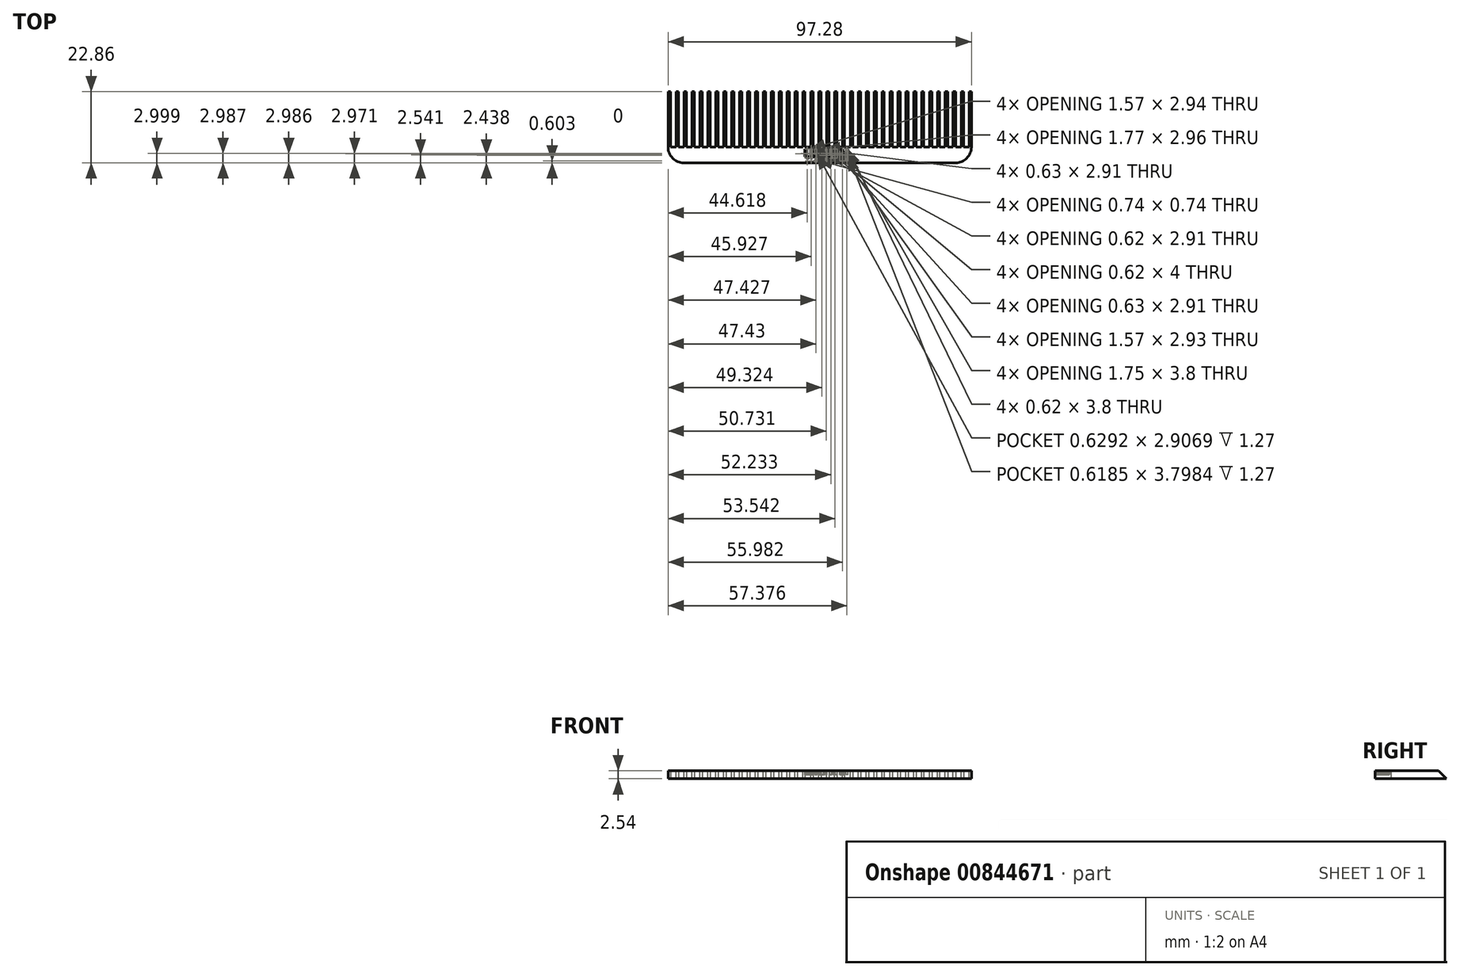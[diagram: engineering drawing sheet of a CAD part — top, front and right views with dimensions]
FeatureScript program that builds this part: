
annotation { "Feature Type Name" : "Feature", "Feature Type Description" : "" }
export const myFeature = defineFeature(function(context is Context, id is Id, definition is map)
    precondition{}
    {
        {
            var Q0;
            Q0=qCreatedBy(makeId("Top.planeOp"),FACE);
            var sketch = newSketch(context, id + "F0", { "sketchPlane" : qUnion([Q0])});
            skLineSegment(sketch, "E0.bottom", {"start": v(46.48, -2.54) * mm, "end": v(-50.8, -2.54) * mm});
            skLineSegment(sketch, "E0.top", {"start": v(46.48, 2.54) * mm, "end": v(-50.8, 2.54) * mm});
            skLineSegment(sketch, "E0.right", {"start": v(-50.8, -2.54) * mm, "end": v(-50.8, 2.54) * mm});
            skPoint(sketch, "E0.middle", {"position": v(0, 0) * mm});
            skLineSegment(sketch, "E1.bottom", {"start": v(-50.8, 2.54) * mm, "end": v(-50.04, 2.54) * mm});
            skLineSegment(sketch, "E1.top", {"start": v(-50.8, 22.86) * mm, "end": v(-50.04, 22.86) * mm});
            skLineSegment(sketch, "E1.left", {"start": v(-50.8, 2.54) * mm, "end": v(-50.8, 22.86) * mm});
            skLineSegment(sketch, "E1.right", {"start": v(-50.04, 2.54) * mm, "end": v(-50.04, 22.86) * mm});
            skLineSegment(sketch, "E2.1.0.0", {"start": v(-47.5, 2.54) * mm, "end": v(-47.5, 22.86) * mm});
            skLineSegment(sketch, "E2.1.0.1", {"start": v(-48.26, 2.54) * mm, "end": v(-48.26, 22.86) * mm});
            skLineSegment(sketch, "E2.1.0.2", {"start": v(-48.26, 22.86) * mm, "end": v(-47.5, 22.86) * mm});
            skLineSegment(sketch, "E2.2.0.0", {"start": v(-44.96, 2.54) * mm, "end": v(-44.96, 22.86) * mm});
            skLineSegment(sketch, "E2.2.0.1", {"start": v(-45.72, 2.54) * mm, "end": v(-45.72, 22.86) * mm});
            skLineSegment(sketch, "E2.2.0.2", {"start": v(-45.72, 22.86) * mm, "end": v(-44.96, 22.86) * mm});
            skLineSegment(sketch, "E2.3.0.0", {"start": v(-42.42, 2.54) * mm, "end": v(-42.42, 22.86) * mm});
            skLineSegment(sketch, "E2.3.0.1", {"start": v(-43.18, 2.54) * mm, "end": v(-43.18, 22.86) * mm});
            skLineSegment(sketch, "E2.3.0.2", {"start": v(-43.18, 22.86) * mm, "end": v(-42.42, 22.86) * mm});
            skLineSegment(sketch, "E2.4.0.0", {"start": v(-39.88, 2.54) * mm, "end": v(-39.88, 22.86) * mm});
            skLineSegment(sketch, "E2.4.0.1", {"start": v(-40.64, 2.54) * mm, "end": v(-40.64, 22.86) * mm});
            skLineSegment(sketch, "E2.4.0.2", {"start": v(-40.64, 22.86) * mm, "end": v(-39.88, 22.86) * mm});
            skLineSegment(sketch, "E2.5.0.0", {"start": v(-37.34, 2.54) * mm, "end": v(-37.34, 22.86) * mm});
            skLineSegment(sketch, "E2.5.0.1", {"start": v(-38.1, 2.54) * mm, "end": v(-38.1, 22.86) * mm});
            skLineSegment(sketch, "E2.5.0.2", {"start": v(-38.1, 22.86) * mm, "end": v(-37.34, 22.86) * mm});
            skLineSegment(sketch, "E2.6.0.0", {"start": v(-34.8, 2.54) * mm, "end": v(-34.8, 22.86) * mm});
            skLineSegment(sketch, "E2.6.0.1", {"start": v(-35.56, 2.54) * mm, "end": v(-35.56, 22.86) * mm});
            skLineSegment(sketch, "E2.6.0.2", {"start": v(-35.56, 22.86) * mm, "end": v(-34.8, 22.86) * mm});
            skLineSegment(sketch, "E2.7.0.0", {"start": v(-32.26, 2.54) * mm, "end": v(-32.26, 22.86) * mm});
            skLineSegment(sketch, "E2.7.0.1", {"start": v(-33.02, 2.54) * mm, "end": v(-33.02, 22.86) * mm});
            skLineSegment(sketch, "E2.7.0.2", {"start": v(-33.02, 22.86) * mm, "end": v(-32.26, 22.86) * mm});
            skLineSegment(sketch, "E2.8.0.0", {"start": v(-29.72, 2.54) * mm, "end": v(-29.72, 22.86) * mm});
            skLineSegment(sketch, "E2.8.0.1", {"start": v(-30.48, 2.54) * mm, "end": v(-30.48, 22.86) * mm});
            skLineSegment(sketch, "E2.8.0.2", {"start": v(-30.48, 22.86) * mm, "end": v(-29.72, 22.86) * mm});
            skLineSegment(sketch, "E2.9.0.0", {"start": v(-27.18, 2.54) * mm, "end": v(-27.18, 22.86) * mm});
            skLineSegment(sketch, "E2.9.0.1", {"start": v(-27.94, 2.54) * mm, "end": v(-27.94, 22.86) * mm});
            skLineSegment(sketch, "E2.9.0.2", {"start": v(-27.94, 22.86) * mm, "end": v(-27.18, 22.86) * mm});
            skLineSegment(sketch, "E2.direction1", {"start": v(-50.04, 2.54) * mm, "end": v(-47.5, 2.54) * mm, "construction": true});
            skLineSegment(sketch, "E3.1.0.0", {"start": v(-25.4, 2.54) * mm, "end": v(-25.4, 22.86) * mm});
            skLineSegment(sketch, "E3.1.0.1", {"start": v(-24.64, 2.54) * mm, "end": v(-24.64, 22.86) * mm});
            skLineSegment(sketch, "E3.1.0.2", {"start": v(-25.4, 22.86) * mm, "end": v(-24.64, 22.86) * mm});
            skLineSegment(sketch, "E3.2.0.0", {"start": v(-22.86, 2.54) * mm, "end": v(-22.86, 22.86) * mm});
            skLineSegment(sketch, "E3.2.0.1", {"start": v(-22.1, 2.54) * mm, "end": v(-22.1, 22.86) * mm});
            skLineSegment(sketch, "E3.2.0.2", {"start": v(-22.86, 22.86) * mm, "end": v(-22.1, 22.86) * mm});
            skLineSegment(sketch, "E3.3.0.0", {"start": v(-20.32, 2.54) * mm, "end": v(-20.32, 22.86) * mm});
            skLineSegment(sketch, "E3.3.0.1", {"start": v(-19.56, 2.54) * mm, "end": v(-19.56, 22.86) * mm});
            skLineSegment(sketch, "E3.3.0.2", {"start": v(-20.32, 22.86) * mm, "end": v(-19.56, 22.86) * mm});
            skLineSegment(sketch, "E3.4.0.0", {"start": v(-17.78, 2.54) * mm, "end": v(-17.78, 22.86) * mm});
            skLineSegment(sketch, "E3.4.0.1", {"start": v(-17.02, 2.54) * mm, "end": v(-17.02, 22.86) * mm});
            skLineSegment(sketch, "E3.4.0.2", {"start": v(-17.78, 22.86) * mm, "end": v(-17.02, 22.86) * mm});
            skLineSegment(sketch, "E3.5.0.0", {"start": v(-15.24, 2.54) * mm, "end": v(-15.24, 22.86) * mm});
            skLineSegment(sketch, "E3.5.0.1", {"start": v(-14.48, 2.54) * mm, "end": v(-14.48, 22.86) * mm});
            skLineSegment(sketch, "E3.5.0.2", {"start": v(-15.24, 22.86) * mm, "end": v(-14.48, 22.86) * mm});
            skLineSegment(sketch, "E3.6.0.0", {"start": v(-12.7, 2.54) * mm, "end": v(-12.7, 22.86) * mm});
            skLineSegment(sketch, "E3.6.0.1", {"start": v(-11.94, 2.54) * mm, "end": v(-11.94, 22.86) * mm});
            skLineSegment(sketch, "E3.6.0.2", {"start": v(-12.7, 22.86) * mm, "end": v(-11.94, 22.86) * mm});
            skLineSegment(sketch, "E3.7.0.0", {"start": v(-10.16, 2.54) * mm, "end": v(-10.16, 22.86) * mm});
            skLineSegment(sketch, "E3.7.0.1", {"start": v(-9.4, 2.54) * mm, "end": v(-9.4, 22.86) * mm});
            skLineSegment(sketch, "E3.7.0.2", {"start": v(-10.16, 22.86) * mm, "end": v(-9.4, 22.86) * mm});
            skLineSegment(sketch, "E3.8.0.0", {"start": v(-7.62, 2.54) * mm, "end": v(-7.62, 22.86) * mm});
            skLineSegment(sketch, "E3.8.0.1", {"start": v(-6.86, 2.54) * mm, "end": v(-6.86, 22.86) * mm});
            skLineSegment(sketch, "E3.8.0.2", {"start": v(-7.62, 22.86) * mm, "end": v(-6.86, 22.86) * mm});
            skLineSegment(sketch, "E3.9.0.0", {"start": v(-5.08, 2.54) * mm, "end": v(-5.08, 22.86) * mm});
            skLineSegment(sketch, "E3.9.0.1", {"start": v(-4.32, 2.54) * mm, "end": v(-4.32, 22.86) * mm});
            skLineSegment(sketch, "E3.9.0.2", {"start": v(-5.08, 22.86) * mm, "end": v(-4.32, 22.86) * mm});
            skLineSegment(sketch, "E3.direction1", {"start": v(-27.94, 2.54) * mm, "end": v(-25.4, 2.54) * mm, "construction": true});
            skLineSegment(sketch, "E4.1.0.0", {"start": v(-1.78, 2.54) * mm, "end": v(-1.78, 22.86) * mm});
            skLineSegment(sketch, "E4.1.0.1", {"start": v(-2.54, 2.54) * mm, "end": v(-2.54, 22.86) * mm});
            skLineSegment(sketch, "E4.1.0.2", {"start": v(-2.54, 22.86) * mm, "end": v(-1.78, 22.86) * mm});
            skLineSegment(sketch, "E4.2.0.0", {"start": v(0.76, 2.54) * mm, "end": v(0.76, 22.86) * mm});
            skLineSegment(sketch, "E4.2.0.1", {"start": v(0, 2.54) * mm, "end": v(0, 22.86) * mm});
            skLineSegment(sketch, "E4.2.0.2", {"start": v(0, 22.86) * mm, "end": v(0.76, 22.86) * mm});
            skLineSegment(sketch, "E4.3.0.0", {"start": v(3.3, 2.54) * mm, "end": v(3.3, 22.86) * mm});
            skLineSegment(sketch, "E4.3.0.1", {"start": v(2.54, 2.54) * mm, "end": v(2.54, 22.86) * mm});
            skLineSegment(sketch, "E4.3.0.2", {"start": v(2.54, 22.86) * mm, "end": v(3.3, 22.86) * mm});
            skLineSegment(sketch, "E4.4.0.0", {"start": v(5.84, 2.54) * mm, "end": v(5.84, 22.86) * mm});
            skLineSegment(sketch, "E4.4.0.1", {"start": v(5.08, 2.54) * mm, "end": v(5.08, 22.86) * mm});
            skLineSegment(sketch, "E4.4.0.2", {"start": v(5.08, 22.86) * mm, "end": v(5.84, 22.86) * mm});
            skLineSegment(sketch, "E4.5.0.0", {"start": v(8.38, 2.54) * mm, "end": v(8.38, 22.86) * mm});
            skLineSegment(sketch, "E4.5.0.1", {"start": v(7.62, 2.54) * mm, "end": v(7.62, 22.86) * mm});
            skLineSegment(sketch, "E4.5.0.2", {"start": v(7.62, 22.86) * mm, "end": v(8.38, 22.86) * mm});
            skLineSegment(sketch, "E4.6.0.0", {"start": v(10.92, 2.54) * mm, "end": v(10.92, 22.86) * mm});
            skLineSegment(sketch, "E4.6.0.1", {"start": v(10.16, 2.54) * mm, "end": v(10.16, 22.86) * mm});
            skLineSegment(sketch, "E4.6.0.2", {"start": v(10.16, 22.86) * mm, "end": v(10.92, 22.86) * mm});
            skLineSegment(sketch, "E4.7.0.0", {"start": v(13.46, 2.54) * mm, "end": v(13.46, 22.86) * mm});
            skLineSegment(sketch, "E4.7.0.1", {"start": v(12.7, 2.54) * mm, "end": v(12.7, 22.86) * mm});
            skLineSegment(sketch, "E4.7.0.2", {"start": v(12.7, 22.86) * mm, "end": v(13.46, 22.86) * mm});
            skLineSegment(sketch, "E4.8.0.0", {"start": v(16, 2.54) * mm, "end": v(16, 22.86) * mm});
            skLineSegment(sketch, "E4.8.0.1", {"start": v(15.24, 2.54) * mm, "end": v(15.24, 22.86) * mm});
            skLineSegment(sketch, "E4.8.0.2", {"start": v(15.24, 22.86) * mm, "end": v(16, 22.86) * mm});
            skLineSegment(sketch, "E4.9.0.0", {"start": v(18.54, 2.54) * mm, "end": v(18.54, 22.86) * mm});
            skLineSegment(sketch, "E4.9.0.1", {"start": v(17.78, 2.54) * mm, "end": v(17.78, 22.86) * mm});
            skLineSegment(sketch, "E4.9.0.2", {"start": v(17.78, 22.86) * mm, "end": v(18.54, 22.86) * mm});
            skLineSegment(sketch, "E4.direction1", {"start": v(-4.32, 2.54) * mm, "end": v(-1.78, 2.54) * mm, "construction": true});
            skLineSegment(sketch, "E5.1.0.0", {"start": v(21.08, 2.54) * mm, "end": v(21.08, 22.86) * mm});
            skLineSegment(sketch, "E5.1.0.1", {"start": v(20.32, 2.54) * mm, "end": v(20.32, 22.86) * mm});
            skLineSegment(sketch, "E5.1.0.2", {"start": v(20.32, 22.86) * mm, "end": v(21.08, 22.86) * mm});
            skLineSegment(sketch, "E5.2.0.0", {"start": v(23.62, 2.54) * mm, "end": v(23.62, 22.86) * mm});
            skLineSegment(sketch, "E5.2.0.1", {"start": v(22.86, 2.54) * mm, "end": v(22.86, 22.86) * mm});
            skLineSegment(sketch, "E5.2.0.2", {"start": v(22.86, 22.86) * mm, "end": v(23.62, 22.86) * mm});
            skLineSegment(sketch, "E5.2.0.3", {"start": v(21.08, 2.54) * mm, "end": v(21.08, 22.86) * mm});
            skLineSegment(sketch, "E5.2.0.4", {"start": v(20.32, 2.54) * mm, "end": v(20.32, 22.86) * mm});
            skLineSegment(sketch, "E5.2.0.5", {"start": v(20.32, 22.86) * mm, "end": v(21.08, 22.86) * mm});
            skLineSegment(sketch, "E5.3.0.0", {"start": v(26.16, 2.54) * mm, "end": v(26.16, 22.86) * mm});
            skLineSegment(sketch, "E5.3.0.1", {"start": v(25.4, 2.54) * mm, "end": v(25.4, 22.86) * mm});
            skLineSegment(sketch, "E5.3.0.2", {"start": v(25.4, 22.86) * mm, "end": v(26.16, 22.86) * mm});
            skLineSegment(sketch, "E5.3.0.3", {"start": v(23.62, 2.54) * mm, "end": v(23.62, 22.86) * mm});
            skLineSegment(sketch, "E5.3.0.4", {"start": v(22.86, 2.54) * mm, "end": v(22.86, 22.86) * mm});
            skLineSegment(sketch, "E5.3.0.5", {"start": v(22.86, 22.86) * mm, "end": v(23.62, 22.86) * mm});
            skLineSegment(sketch, "E5.3.0.6", {"start": v(21.08, 2.54) * mm, "end": v(21.08, 22.86) * mm});
            skLineSegment(sketch, "E5.3.0.7", {"start": v(20.32, 2.54) * mm, "end": v(20.32, 22.86) * mm});
            skLineSegment(sketch, "E5.3.0.8", {"start": v(20.32, 22.86) * mm, "end": v(21.08, 22.86) * mm});
            skLineSegment(sketch, "E5.4.0.0", {"start": v(28.7, 2.54) * mm, "end": v(28.7, 22.86) * mm});
            skLineSegment(sketch, "E5.4.0.1", {"start": v(27.94, 2.54) * mm, "end": v(27.94, 22.86) * mm});
            skLineSegment(sketch, "E5.4.0.2", {"start": v(27.94, 22.86) * mm, "end": v(28.7, 22.86) * mm});
            skLineSegment(sketch, "E5.4.0.3", {"start": v(26.16, 2.54) * mm, "end": v(26.16, 22.86) * mm});
            skLineSegment(sketch, "E5.4.0.4", {"start": v(25.4, 2.54) * mm, "end": v(25.4, 22.86) * mm});
            skLineSegment(sketch, "E5.4.0.5", {"start": v(25.4, 22.86) * mm, "end": v(26.16, 22.86) * mm});
            skLineSegment(sketch, "E5.4.0.6", {"start": v(23.62, 2.54) * mm, "end": v(23.62, 22.86) * mm});
            skLineSegment(sketch, "E5.4.0.7", {"start": v(22.86, 2.54) * mm, "end": v(22.86, 22.86) * mm});
            skLineSegment(sketch, "E5.4.0.8", {"start": v(22.86, 22.86) * mm, "end": v(23.62, 22.86) * mm});
            skLineSegment(sketch, "E5.5.0.0", {"start": v(31.24, 2.54) * mm, "end": v(31.24, 22.86) * mm});
            skLineSegment(sketch, "E5.5.0.1", {"start": v(30.48, 2.54) * mm, "end": v(30.48, 22.86) * mm});
            skLineSegment(sketch, "E5.5.0.2", {"start": v(30.48, 22.86) * mm, "end": v(31.24, 22.86) * mm});
            skLineSegment(sketch, "E5.5.0.3", {"start": v(28.7, 2.54) * mm, "end": v(28.7, 22.86) * mm});
            skLineSegment(sketch, "E5.5.0.4", {"start": v(27.94, 2.54) * mm, "end": v(27.94, 22.86) * mm});
            skLineSegment(sketch, "E5.5.0.5", {"start": v(27.94, 22.86) * mm, "end": v(28.7, 22.86) * mm});
            skLineSegment(sketch, "E5.5.0.6", {"start": v(26.16, 2.54) * mm, "end": v(26.16, 22.86) * mm});
            skLineSegment(sketch, "E5.5.0.7", {"start": v(25.4, 2.54) * mm, "end": v(25.4, 22.86) * mm});
            skLineSegment(sketch, "E5.5.0.8", {"start": v(25.4, 22.86) * mm, "end": v(26.16, 22.86) * mm});
            skLineSegment(sketch, "E5.6.0.0", {"start": v(33.78, 2.54) * mm, "end": v(33.78, 22.86) * mm});
            skLineSegment(sketch, "E5.6.0.1", {"start": v(33.02, 2.54) * mm, "end": v(33.02, 22.86) * mm});
            skLineSegment(sketch, "E5.6.0.2", {"start": v(33.02, 22.86) * mm, "end": v(33.78, 22.86) * mm});
            skLineSegment(sketch, "E5.6.0.3", {"start": v(31.24, 2.54) * mm, "end": v(31.24, 22.86) * mm});
            skLineSegment(sketch, "E5.6.0.4", {"start": v(30.48, 2.54) * mm, "end": v(30.48, 22.86) * mm});
            skLineSegment(sketch, "E5.6.0.5", {"start": v(30.48, 22.86) * mm, "end": v(31.24, 22.86) * mm});
            skLineSegment(sketch, "E5.6.0.6", {"start": v(28.7, 2.54) * mm, "end": v(28.7, 22.86) * mm});
            skLineSegment(sketch, "E5.6.0.7", {"start": v(27.94, 2.54) * mm, "end": v(27.94, 22.86) * mm});
            skLineSegment(sketch, "E5.6.0.8", {"start": v(27.94, 22.86) * mm, "end": v(28.7, 22.86) * mm});
            skLineSegment(sketch, "E5.7.0.0", {"start": v(36.32, 2.54) * mm, "end": v(36.32, 22.86) * mm});
            skLineSegment(sketch, "E5.7.0.1", {"start": v(35.56, 2.54) * mm, "end": v(35.56, 22.86) * mm});
            skLineSegment(sketch, "E5.7.0.2", {"start": v(35.56, 22.86) * mm, "end": v(36.32, 22.86) * mm});
            skLineSegment(sketch, "E5.7.0.3", {"start": v(33.78, 2.54) * mm, "end": v(33.78, 22.86) * mm});
            skLineSegment(sketch, "E5.7.0.4", {"start": v(33.02, 2.54) * mm, "end": v(33.02, 22.86) * mm});
            skLineSegment(sketch, "E5.7.0.5", {"start": v(33.02, 22.86) * mm, "end": v(33.78, 22.86) * mm});
            skLineSegment(sketch, "E5.7.0.6", {"start": v(31.24, 2.54) * mm, "end": v(31.24, 22.86) * mm});
            skLineSegment(sketch, "E5.7.0.7", {"start": v(30.48, 2.54) * mm, "end": v(30.48, 22.86) * mm});
            skLineSegment(sketch, "E5.7.0.8", {"start": v(30.48, 22.86) * mm, "end": v(31.24, 22.86) * mm});
            skLineSegment(sketch, "E5.8.0.0", {"start": v(38.86, 2.54) * mm, "end": v(38.86, 22.86) * mm});
            skLineSegment(sketch, "E5.8.0.1", {"start": v(38.1, 2.54) * mm, "end": v(38.1, 22.86) * mm});
            skLineSegment(sketch, "E5.8.0.2", {"start": v(38.1, 22.86) * mm, "end": v(38.86, 22.86) * mm});
            skLineSegment(sketch, "E5.8.0.3", {"start": v(36.32, 2.54) * mm, "end": v(36.32, 22.86) * mm});
            skLineSegment(sketch, "E5.8.0.4", {"start": v(35.56, 2.54) * mm, "end": v(35.56, 22.86) * mm});
            skLineSegment(sketch, "E5.8.0.5", {"start": v(35.56, 22.86) * mm, "end": v(36.32, 22.86) * mm});
            skLineSegment(sketch, "E5.8.0.6", {"start": v(33.78, 2.54) * mm, "end": v(33.78, 22.86) * mm});
            skLineSegment(sketch, "E5.8.0.7", {"start": v(33.02, 2.54) * mm, "end": v(33.02, 22.86) * mm});
            skLineSegment(sketch, "E5.8.0.8", {"start": v(33.02, 22.86) * mm, "end": v(33.78, 22.86) * mm});
            skLineSegment(sketch, "E5.9.0.0", {"start": v(41.4, 2.54) * mm, "end": v(41.4, 22.86) * mm});
            skLineSegment(sketch, "E5.9.0.1", {"start": v(40.64, 2.54) * mm, "end": v(40.64, 22.86) * mm});
            skLineSegment(sketch, "E5.9.0.2", {"start": v(40.64, 22.86) * mm, "end": v(41.4, 22.86) * mm});
            skLineSegment(sketch, "E5.9.0.3", {"start": v(38.86, 2.54) * mm, "end": v(38.86, 22.86) * mm});
            skLineSegment(sketch, "E5.9.0.4", {"start": v(38.1, 2.54) * mm, "end": v(38.1, 22.86) * mm});
            skLineSegment(sketch, "E5.9.0.5", {"start": v(38.1, 22.86) * mm, "end": v(38.86, 22.86) * mm});
            skLineSegment(sketch, "E5.9.0.6", {"start": v(36.32, 2.54) * mm, "end": v(36.32, 22.86) * mm});
            skLineSegment(sketch, "E5.9.0.7", {"start": v(35.56, 2.54) * mm, "end": v(35.56, 22.86) * mm});
            skLineSegment(sketch, "E5.9.0.8", {"start": v(35.56, 22.86) * mm, "end": v(36.32, 22.86) * mm});
            skLineSegment(sketch, "E5.direction1", {"start": v(18.54, 2.54) * mm, "end": v(21.08, 2.54) * mm, "construction": true});
            skLineSegment(sketch, "E6.1.0.0", {"start": v(43.94, 2.54) * mm, "end": v(43.94, 22.86) * mm});
            skLineSegment(sketch, "E6.1.0.1", {"start": v(43.18, 2.54) * mm, "end": v(43.18, 22.86) * mm});
            skLineSegment(sketch, "E6.1.0.2", {"start": v(43.18, 22.86) * mm, "end": v(43.94, 22.86) * mm});
            skLineSegment(sketch, "E6.2.0.0", {"start": v(46.48, 2.54) * mm, "end": v(46.48, 22.86) * mm});
            skLineSegment(sketch, "E6.2.0.1", {"start": v(45.72, 2.54) * mm, "end": v(45.72, 22.86) * mm});
            skLineSegment(sketch, "E6.2.0.2", {"start": v(45.72, 22.86) * mm, "end": v(46.48, 22.86) * mm});
            skLineSegment(sketch, "E6.direction1", {"start": v(41.4, 2.54) * mm, "end": v(43.94, 2.54) * mm, "construction": true});
            skLineSegment(sketch, "E7", {"start": v(46.48, 2.54) * mm, "end": v(46.48, -2.54) * mm});
            skPoint(sketch, "E0.left.end.orphan", {"position": v(50.8, 2.54) * mm});
            skPoint(sketch, "E8.orphan", {"position": v(50.8, -2.54) * mm});
            skSolve(sketch);
        }
        {
            var Q0;
            {var subQ0=sQuery(id+"F0.wireOp",EDGE,"E4.4.0.0");Q0=makeQuery(id+"F0.imprint","IMPRINT",FACE,{"disambiguationData":[TD([[makeQuery(id+"F0.imprint","IMPRINT",EDGE,{"derivedFrom":subQ0}),1.0]])]});}
            var Q1;
            {var subQ0=sQuery(id+"F0.wireOp",EDGE,"E6.1.0.0");Q1=makeQuery(id+"F0.imprint","IMPRINT",FACE,{"disambiguationData":[TD([[makeQuery(id+"F0.imprint","IMPRINT",EDGE,{"derivedFrom":subQ0}),1.0]])]});}
            var Q2;
            {var subQ0=sQuery(id+"F0.wireOp",EDGE,"E3.2.0.0");Q2=makeQuery(id+"F0.imprint","IMPRINT",FACE,{"disambiguationData":[TD([[makeQuery(id+"F0.imprint","IMPRINT",EDGE,{"derivedFrom":subQ0}),-1.0]])]});}
            var Q3;
            {var subQ0=sQuery(id+"F0.wireOp",EDGE,"E6.2.0.0");Q3=makeQuery(id+"F0.imprint","IMPRINT",FACE,{"disambiguationData":[TD([[makeQuery(id+"F0.imprint","IMPRINT",EDGE,{"derivedFrom":subQ0}),1.0]])]});}
            var Q4;
            {var subQ0=sQuery(id+"F0.wireOp",EDGE,"E2.3.0.0");Q4=makeQuery(id+"F0.imprint","IMPRINT",FACE,{"disambiguationData":[TD([[makeQuery(id+"F0.imprint","IMPRINT",EDGE,{"derivedFrom":subQ0}),1.0]])]});}
            var Q5;
            {var subQ0=sQuery(id+"F0.wireOp",EDGE,"E5.8.0.0");Q5=makeQuery(id+"F0.imprint","IMPRINT",FACE,{"disambiguationData":[TD([[makeQuery(id+"F0.imprint","IMPRINT",EDGE,{"derivedFrom":subQ0}),1.0]])]});}
            var Q6;
            {var subQ0=sQuery(id+"F0.wireOp",EDGE,"E2.6.0.0");Q6=makeQuery(id+"F0.imprint","IMPRINT",FACE,{"disambiguationData":[TD([[makeQuery(id+"F0.imprint","IMPRINT",EDGE,{"derivedFrom":subQ0}),1.0]])]});}
            var Q7;
            Q7=makeQuery(id+"F0.imprint","IMPRINT",FACE,{"disambiguationData":[TD([[makeQuery(id+"F0.imprint","IMPRINT",EDGE,{"derivedFrom":sQuery(id+"F0.wireOp",EDGE,"E1.top")}),-1.0]])]});
            var Q8;
            {var subQ0=sQuery(id+"F0.wireOp",EDGE,"E5.6.0.0");Q8=makeQuery(id+"F0.imprint","IMPRINT",FACE,{"disambiguationData":[TD([[makeQuery(id+"F0.imprint","IMPRINT",EDGE,{"derivedFrom":subQ0}),1.0]])]});}
            var Q9;
            {var subQ0=sQuery(id+"F0.wireOp",EDGE,"E3.1.0.0");Q9=makeQuery(id+"F0.imprint","IMPRINT",FACE,{"disambiguationData":[TD([[makeQuery(id+"F0.imprint","IMPRINT",EDGE,{"derivedFrom":subQ0}),-1.0]])]});}
            var Q10;
            {var subQ0=sQuery(id+"F0.wireOp",EDGE,"E3.3.0.0");Q10=makeQuery(id+"F0.imprint","IMPRINT",FACE,{"disambiguationData":[TD([[makeQuery(id+"F0.imprint","IMPRINT",EDGE,{"derivedFrom":subQ0}),-1.0]])]});}
            var Q11;
            {var subQ2=sQuery(id+"F0.wireOp",EDGE,"E2.1.0.0");Q11=makeQuery(id+"F0.imprint","IMPRINT",FACE,{"disambiguationData":[TD([[makeQuery(id+"F0.imprint","IMPRINT",EDGE,{"derivedFrom":subQ2}),1.0]])]});}
            var Q12;
            {var subQ0=sQuery(id+"F0.wireOp",EDGE,"E2.9.0.0");Q12=makeQuery(id+"F0.imprint","IMPRINT",FACE,{"disambiguationData":[TD([[makeQuery(id+"F0.imprint","IMPRINT",EDGE,{"derivedFrom":subQ0}),1.0]])]});}
            var Q13;
            {var subQ0=sQuery(id+"F0.wireOp",EDGE,"E2.4.0.0");Q13=makeQuery(id+"F0.imprint","IMPRINT",FACE,{"disambiguationData":[TD([[makeQuery(id+"F0.imprint","IMPRINT",EDGE,{"derivedFrom":subQ0}),1.0]])]});}
            var Q14;
            Q14=makeQuery(id+"F0.imprint","IMPRINT",FACE,{"disambiguationData":[TD([[makeQuery(id+"F0.imprint","IMPRINT",EDGE,{"derivedFrom":sQuery(id+"F0.wireOp",EDGE,"E0.bottom")}),-1.0]])]});
            var Q15;
            {var subQ0=sQuery(id+"F0.wireOp",EDGE,"E2.5.0.0");Q15=makeQuery(id+"F0.imprint","IMPRINT",FACE,{"disambiguationData":[TD([[makeQuery(id+"F0.imprint","IMPRINT",EDGE,{"derivedFrom":subQ0}),1.0]])]});}
            var Q16;
            {var subQ0=sQuery(id+"F0.wireOp",EDGE,"E2.8.0.0");Q16=makeQuery(id+"F0.imprint","IMPRINT",FACE,{"disambiguationData":[TD([[makeQuery(id+"F0.imprint","IMPRINT",EDGE,{"derivedFrom":subQ0}),1.0]])]});}
            var Q17;
            {var subQ0=sQuery(id+"F0.wireOp",EDGE,"E2.2.0.0");Q17=makeQuery(id+"F0.imprint","IMPRINT",FACE,{"disambiguationData":[TD([[makeQuery(id+"F0.imprint","IMPRINT",EDGE,{"derivedFrom":subQ0}),1.0]])]});}
            var Q18;
            {var subQ0=sQuery(id+"F0.wireOp",EDGE,"E3.4.0.0");Q18=makeQuery(id+"F0.imprint","IMPRINT",FACE,{"disambiguationData":[TD([[makeQuery(id+"F0.imprint","IMPRINT",EDGE,{"derivedFrom":subQ0}),-1.0]])]});}
            var Q19;
            {var subQ0=sQuery(id+"F0.wireOp",EDGE,"E4.7.0.0");Q19=makeQuery(id+"F0.imprint","IMPRINT",FACE,{"disambiguationData":[TD([[makeQuery(id+"F0.imprint","IMPRINT",EDGE,{"derivedFrom":subQ0}),1.0]])]});}
            var Q20;
            {var subQ2=sQuery(id+"F0.wireOp",EDGE,"E2.7.0.0");Q20=makeQuery(id+"F0.imprint","IMPRINT",FACE,{"disambiguationData":[TD([[makeQuery(id+"F0.imprint","IMPRINT",EDGE,{"derivedFrom":subQ2}),1.0]])]});}
            var Q21;
            {var subQ0=sQuery(id+"F0.wireOp",EDGE,"E5.7.0.0");Q21=makeQuery(id+"F0.imprint","IMPRINT",FACE,{"disambiguationData":[TD([[makeQuery(id+"F0.imprint","IMPRINT",EDGE,{"derivedFrom":subQ0}),1.0]])]});}
            var Q22;
            {var subQ0=sQuery(id+"F0.wireOp",EDGE,"E5.5.0.0");Q22=makeQuery(id+"F0.imprint","IMPRINT",FACE,{"disambiguationData":[TD([[makeQuery(id+"F0.imprint","IMPRINT",EDGE,{"derivedFrom":subQ0}),1.0]])]});}
            var Q23;
            {var subQ0=sQuery(id+"F0.wireOp",EDGE,"E4.8.0.0");Q23=makeQuery(id+"F0.imprint","IMPRINT",FACE,{"disambiguationData":[TD([[makeQuery(id+"F0.imprint","IMPRINT",EDGE,{"derivedFrom":subQ0}),1.0]])]});}
            var Q24;
            {var subQ0=sQuery(id+"F0.wireOp",EDGE,"E3.7.0.0");Q24=makeQuery(id+"F0.imprint","IMPRINT",FACE,{"disambiguationData":[TD([[makeQuery(id+"F0.imprint","IMPRINT",EDGE,{"derivedFrom":subQ0}),-1.0]])]});}
            var Q25;
            {var subQ0=sQuery(id+"F0.wireOp",EDGE,"E3.9.0.0");Q25=makeQuery(id+"F0.imprint","IMPRINT",FACE,{"disambiguationData":[TD([[makeQuery(id+"F0.imprint","IMPRINT",EDGE,{"derivedFrom":subQ0}),-1.0]])]});}
            var Q26;
            {var subQ0=sQuery(id+"F0.wireOp",EDGE,"E4.3.0.0");Q26=makeQuery(id+"F0.imprint","IMPRINT",FACE,{"disambiguationData":[TD([[makeQuery(id+"F0.imprint","IMPRINT",EDGE,{"derivedFrom":subQ0}),1.0]])]});}
            var Q27;
            {var subQ0=sQuery(id+"F0.wireOp",EDGE,"E5.3.0.0");Q27=makeQuery(id+"F0.imprint","IMPRINT",FACE,{"disambiguationData":[TD([[makeQuery(id+"F0.imprint","IMPRINT",EDGE,{"derivedFrom":subQ0}),1.0]])]});}
            var Q28;
            {var subQ0=sQuery(id+"F0.wireOp",EDGE,"E5.9.0.0");Q28=makeQuery(id+"F0.imprint","IMPRINT",FACE,{"disambiguationData":[TD([[makeQuery(id+"F0.imprint","IMPRINT",EDGE,{"derivedFrom":subQ0}),1.0]])]});}
            var Q29;
            {var subQ0=sQuery(id+"F0.wireOp",EDGE,"E5.1.0.0");Q29=makeQuery(id+"F0.imprint","IMPRINT",FACE,{"disambiguationData":[TD([[makeQuery(id+"F0.imprint","IMPRINT",EDGE,{"derivedFrom":subQ0}),1.0]])]});}
            var Q30;
            {var subQ0=sQuery(id+"F0.wireOp",EDGE,"E5.2.0.0");Q30=makeQuery(id+"F0.imprint","IMPRINT",FACE,{"disambiguationData":[TD([[makeQuery(id+"F0.imprint","IMPRINT",EDGE,{"derivedFrom":subQ0}),1.0]])]});}
            var Q31;
            {var subQ0=sQuery(id+"F0.wireOp",EDGE,"E4.5.0.0");Q31=makeQuery(id+"F0.imprint","IMPRINT",FACE,{"disambiguationData":[TD([[makeQuery(id+"F0.imprint","IMPRINT",EDGE,{"derivedFrom":subQ0}),1.0]])]});}
            var Q32;
            {var subQ0=sQuery(id+"F0.wireOp",EDGE,"E4.6.0.0");Q32=makeQuery(id+"F0.imprint","IMPRINT",FACE,{"disambiguationData":[TD([[makeQuery(id+"F0.imprint","IMPRINT",EDGE,{"derivedFrom":subQ0}),1.0]])]});}
            var Q33;
            {var subQ0=sQuery(id+"F0.wireOp",EDGE,"E4.9.0.0");Q33=makeQuery(id+"F0.imprint","IMPRINT",FACE,{"disambiguationData":[TD([[makeQuery(id+"F0.imprint","IMPRINT",EDGE,{"derivedFrom":subQ0}),1.0]])]});}
            var Q34;
            {var subQ0=sQuery(id+"F0.wireOp",EDGE,"E3.6.0.0");Q34=makeQuery(id+"F0.imprint","IMPRINT",FACE,{"disambiguationData":[TD([[makeQuery(id+"F0.imprint","IMPRINT",EDGE,{"derivedFrom":subQ0}),-1.0]])]});}
            var Q35;
            {var subQ0=sQuery(id+"F0.wireOp",EDGE,"E3.5.0.0");Q35=makeQuery(id+"F0.imprint","IMPRINT",FACE,{"disambiguationData":[TD([[makeQuery(id+"F0.imprint","IMPRINT",EDGE,{"derivedFrom":subQ0}),-1.0]])]});}
            var Q36;
            {var subQ0=sQuery(id+"F0.wireOp",EDGE,"E4.1.0.0");Q36=makeQuery(id+"F0.imprint","IMPRINT",FACE,{"disambiguationData":[TD([[makeQuery(id+"F0.imprint","IMPRINT",EDGE,{"derivedFrom":subQ0}),1.0]])]});}
            var Q37;
            {var subQ0=sQuery(id+"F0.wireOp",EDGE,"E3.8.0.0");Q37=makeQuery(id+"F0.imprint","IMPRINT",FACE,{"disambiguationData":[TD([[makeQuery(id+"F0.imprint","IMPRINT",EDGE,{"derivedFrom":subQ0}),-1.0]])]});}
            var Q38;
            {var subQ0=sQuery(id+"F0.wireOp",EDGE,"E4.2.0.0");Q38=makeQuery(id+"F0.imprint","IMPRINT",FACE,{"disambiguationData":[TD([[makeQuery(id+"F0.imprint","IMPRINT",EDGE,{"derivedFrom":subQ0}),1.0]])]});}
            var Q39;
            {var subQ0=sQuery(id+"F0.wireOp",EDGE,"E5.4.0.0");Q39=makeQuery(id+"F0.imprint","IMPRINT",FACE,{"disambiguationData":[TD([[makeQuery(id+"F0.imprint","IMPRINT",EDGE,{"derivedFrom":subQ0}),1.0]])]});}
            extrude(context, id + "F1", {"entities" : qUnion([Q0, Q1, Q2, Q3, Q4, Q5, Q6, Q7, Q8, Q9, Q10, Q11, Q12, Q13, Q14, Q15, Q16, Q17, Q18, Q19, Q20, Q21, Q22, Q23, Q24, Q25, Q26, Q27, Q28, Q29, Q30, Q31, Q32, Q33, Q34, Q35, Q36, Q37, Q38, Q39]), "depth" : 2.54 * mm, "offsetDistance" : 25.4 * mm});
        }
        {
            var Q0;
            Q0=makeQuery(id+"F1.opExtrude","SWEPT_EDGE",EDGE,{"disambiguationData":[OSD([sQuery(id+"F0.wireOp",EDGE,"E0.bottom"),sQuery(id+"F0.wireOp",EDGE,"E0.right")])]});
            var Q1;
            Q1=makeQuery(id+"F1.opExtrude","SWEPT_EDGE",EDGE,{"disambiguationData":[OSD([sQuery(id+"F0.wireOp",EDGE,"E0.bottom"),sQuery(id+"F0.wireOp",EDGE,"E7")])]});
            fillet(context, id + "F2", {"entities" : qUnion([Q0, Q1]), "radius" : 5.08 * mm, "tangentPropagation" : true, "allowEdgeOverflow" : false});
        }
        {
            var Q0;
            Q0=makeQuery(id+"F1.opExtrude","CAP_FACE",FACE,{"disambiguationData":[OSD([sQuery(id+"F0.wireOp",EDGE,"E0.bottom"),sQuery(id+"F0.wireOp",EDGE,"E0.top"),sQuery(id+"F0.wireOp",EDGE,"E0.right"),sQuery(id+"F0.wireOp",EDGE,"E1.top"),sQuery(id+"F0.wireOp",EDGE,"E1.left"),sQuery(id+"F0.wireOp",EDGE,"E1.right"),sQuery(id+"F0.wireOp",EDGE,"E2.1.0.0"),sQuery(id+"F0.wireOp",EDGE,"E2.1.0.1"),sQuery(id+"F0.wireOp",EDGE,"E2.1.0.2"),sQuery(id+"F0.wireOp",EDGE,"E2.2.0.0"),sQuery(id+"F0.wireOp",EDGE,"E2.2.0.1"),sQuery(id+"F0.wireOp",EDGE,"E2.2.0.2"),sQuery(id+"F0.wireOp",EDGE,"E2.3.0.0"),sQuery(id+"F0.wireOp",EDGE,"E2.3.0.1"),sQuery(id+"F0.wireOp",EDGE,"E2.3.0.2"),sQuery(id+"F0.wireOp",EDGE,"E2.4.0.0"),sQuery(id+"F0.wireOp",EDGE,"E2.4.0.1"),sQuery(id+"F0.wireOp",EDGE,"E2.4.0.2"),sQuery(id+"F0.wireOp",EDGE,"E2.5.0.0"),sQuery(id+"F0.wireOp",EDGE,"E2.5.0.1"),sQuery(id+"F0.wireOp",EDGE,"E2.5.0.2"),sQuery(id+"F0.wireOp",EDGE,"E2.6.0.0"),sQuery(id+"F0.wireOp",EDGE,"E2.6.0.1"),sQuery(id+"F0.wireOp",EDGE,"E2.6.0.2"),sQuery(id+"F0.wireOp",EDGE,"E2.7.0.0"),sQuery(id+"F0.wireOp",EDGE,"E2.7.0.1"),sQuery(id+"F0.wireOp",EDGE,"E2.7.0.2"),sQuery(id+"F0.wireOp",EDGE,"E2.8.0.0"),sQuery(id+"F0.wireOp",EDGE,"E2.8.0.1"),sQuery(id+"F0.wireOp",EDGE,"E2.8.0.2"),sQuery(id+"F0.wireOp",EDGE,"E2.9.0.0"),sQuery(id+"F0.wireOp",EDGE,"E2.9.0.1"),sQuery(id+"F0.wireOp",EDGE,"E2.9.0.2"),sQuery(id+"F0.wireOp",EDGE,"E3.1.0.0"),sQuery(id+"F0.wireOp",EDGE,"E3.1.0.1"),sQuery(id+"F0.wireOp",EDGE,"E3.1.0.2"),sQuery(id+"F0.wireOp",EDGE,"E3.2.0.0"),sQuery(id+"F0.wireOp",EDGE,"E3.2.0.1"),sQuery(id+"F0.wireOp",EDGE,"E3.2.0.2"),sQuery(id+"F0.wireOp",EDGE,"E3.3.0.0"),sQuery(id+"F0.wireOp",EDGE,"E3.3.0.1"),sQuery(id+"F0.wireOp",EDGE,"E3.3.0.2"),sQuery(id+"F0.wireOp",EDGE,"E3.4.0.0"),sQuery(id+"F0.wireOp",EDGE,"E3.4.0.1"),sQuery(id+"F0.wireOp",EDGE,"E3.4.0.2"),sQuery(id+"F0.wireOp",EDGE,"E3.5.0.0"),sQuery(id+"F0.wireOp",EDGE,"E3.5.0.1"),sQuery(id+"F0.wireOp",EDGE,"E3.5.0.2"),sQuery(id+"F0.wireOp",EDGE,"E3.6.0.0"),sQuery(id+"F0.wireOp",EDGE,"E3.6.0.1"),sQuery(id+"F0.wireOp",EDGE,"E3.6.0.2"),sQuery(id+"F0.wireOp",EDGE,"E3.7.0.0"),sQuery(id+"F0.wireOp",EDGE,"E3.7.0.1"),sQuery(id+"F0.wireOp",EDGE,"E3.7.0.2"),sQuery(id+"F0.wireOp",EDGE,"E3.8.0.0"),sQuery(id+"F0.wireOp",EDGE,"E3.8.0.1"),sQuery(id+"F0.wireOp",EDGE,"E3.8.0.2"),sQuery(id+"F0.wireOp",EDGE,"E3.9.0.0"),sQuery(id+"F0.wireOp",EDGE,"E3.9.0.1"),sQuery(id+"F0.wireOp",EDGE,"E3.9.0.2"),sQuery(id+"F0.wireOp",EDGE,"E4.1.0.0"),sQuery(id+"F0.wireOp",EDGE,"E4.1.0.1"),sQuery(id+"F0.wireOp",EDGE,"E4.1.0.2"),sQuery(id+"F0.wireOp",EDGE,"E4.2.0.0"),sQuery(id+"F0.wireOp",EDGE,"E4.2.0.1"),sQuery(id+"F0.wireOp",EDGE,"E4.2.0.2"),sQuery(id+"F0.wireOp",EDGE,"E4.3.0.0"),sQuery(id+"F0.wireOp",EDGE,"E4.3.0.1"),sQuery(id+"F0.wireOp",EDGE,"E4.3.0.2"),sQuery(id+"F0.wireOp",EDGE,"E4.4.0.0"),sQuery(id+"F0.wireOp",EDGE,"E4.4.0.1"),sQuery(id+"F0.wireOp",EDGE,"E4.4.0.2"),sQuery(id+"F0.wireOp",EDGE,"E4.5.0.0"),sQuery(id+"F0.wireOp",EDGE,"E4.5.0.1"),sQuery(id+"F0.wireOp",EDGE,"E4.5.0.2"),sQuery(id+"F0.wireOp",EDGE,"E4.6.0.0"),sQuery(id+"F0.wireOp",EDGE,"E4.6.0.1"),sQuery(id+"F0.wireOp",EDGE,"E4.6.0.2"),sQuery(id+"F0.wireOp",EDGE,"E4.7.0.0"),sQuery(id+"F0.wireOp",EDGE,"E4.7.0.1"),sQuery(id+"F0.wireOp",EDGE,"E4.7.0.2"),sQuery(id+"F0.wireOp",EDGE,"E4.8.0.0"),sQuery(id+"F0.wireOp",EDGE,"E4.8.0.1"),sQuery(id+"F0.wireOp",EDGE,"E4.8.0.2"),sQuery(id+"F0.wireOp",EDGE,"E4.9.0.0"),sQuery(id+"F0.wireOp",EDGE,"E4.9.0.1"),sQuery(id+"F0.wireOp",EDGE,"E4.9.0.2"),sQuery(id+"F0.wireOp",EDGE,"E5.1.0.0"),sQuery(id+"F0.wireOp",EDGE,"E5.1.0.1"),sQuery(id+"F0.wireOp",EDGE,"E5.1.0.2"),sQuery(id+"F0.wireOp",EDGE,"E5.2.0.0"),sQuery(id+"F0.wireOp",EDGE,"E5.2.0.1"),sQuery(id+"F0.wireOp",EDGE,"E5.2.0.2"),sQuery(id+"F0.wireOp",EDGE,"E5.3.0.0"),sQuery(id+"F0.wireOp",EDGE,"E5.3.0.1"),sQuery(id+"F0.wireOp",EDGE,"E5.3.0.2"),sQuery(id+"F0.wireOp",EDGE,"E5.4.0.0"),sQuery(id+"F0.wireOp",EDGE,"E5.4.0.1"),sQuery(id+"F0.wireOp",EDGE,"E5.4.0.2"),sQuery(id+"F0.wireOp",EDGE,"E5.5.0.0"),sQuery(id+"F0.wireOp",EDGE,"E5.5.0.1"),sQuery(id+"F0.wireOp",EDGE,"E5.5.0.2"),sQuery(id+"F0.wireOp",EDGE,"E5.6.0.0"),sQuery(id+"F0.wireOp",EDGE,"E5.6.0.1"),sQuery(id+"F0.wireOp",EDGE,"E5.6.0.2"),sQuery(id+"F0.wireOp",EDGE,"E5.7.0.0"),sQuery(id+"F0.wireOp",EDGE,"E5.7.0.1"),sQuery(id+"F0.wireOp",EDGE,"E5.7.0.2"),sQuery(id+"F0.wireOp",EDGE,"E5.8.0.0"),sQuery(id+"F0.wireOp",EDGE,"E5.8.0.1"),sQuery(id+"F0.wireOp",EDGE,"E5.8.0.2"),sQuery(id+"F0.wireOp",EDGE,"E5.9.0.0"),sQuery(id+"F0.wireOp",EDGE,"E5.9.0.1"),sQuery(id+"F0.wireOp",EDGE,"E5.9.0.2"),sQuery(id+"F0.wireOp",EDGE,"E6.1.0.0"),sQuery(id+"F0.wireOp",EDGE,"E6.1.0.1"),sQuery(id+"F0.wireOp",EDGE,"E6.1.0.2"),sQuery(id+"F0.wireOp",EDGE,"E6.2.0.0"),sQuery(id+"F0.wireOp",EDGE,"E6.2.0.1"),sQuery(id+"F0.wireOp",EDGE,"E6.2.0.2"),sQuery(id+"F0.wireOp",EDGE,"E7")])],"isStart":false});
            var sketch = newSketch(context, id + "F3", { "sketchPlane" : qUnion([Q0])});
            skText(sketch, "E9", { "text": "Rubin", "fontName": "AllertaStencil-Regular.ttf"});
            skPoint(sketch, "E10", {"position": v(0, 0) * mm});
            const initialGuessF3  = {"E9": [0.00735, 0.0019, -1, 0, 0.0038]};
            skSetInitialGuess(sketch, initialGuessF3);
            skSolve(sketch);
        }
        {
            var Q0;
            Q0 = qSketchRegion(id + "F3", true);
            extrude(context, id + "F4", {"entities" : qUnion([Q0]), "operationType" : NewBodyOperationType.REMOVE, "oppositeDirection" : true, "depth" : 1.27 * mm, "offsetDistance" : 25.4 * mm});
        }
        {
            var Q0;
            Q0=makeQuery(id+"F1.opExtrude","CAP_EDGE",EDGE,{"disambiguationData":[OSD([sQuery(id+"F0.wireOp",EDGE,"E1.top")])],"isStart":false});
            var Q1;
            Q1=makeQuery(id+"F1.opExtrude","CAP_EDGE",EDGE,{"disambiguationData":[OSD([sQuery(id+"F0.wireOp",EDGE,"E2.1.0.2")])],"isStart":false});
            chamfer(context, id + "F5", {"entities" : qUnion([Q0, Q1]), "width" : 5.08 * mm, "tangentPropagation" : true});
        }
        {
            var Q0;
            Q0=makeQuery(id+"F1.opExtrude","CAP_EDGE",EDGE,{"disambiguationData":[OSD([sQuery(id+"F0.wireOp",EDGE,"E2.2.0.2")])],"isStart":false});
            var Q1;
            Q1=makeQuery(id+"F1.opExtrude","CAP_EDGE",EDGE,{"disambiguationData":[OSD([sQuery(id+"F0.wireOp",EDGE,"E2.3.0.2")])],"isStart":false});
            var Q2;
            Q2=makeQuery(id+"F1.opExtrude","CAP_EDGE",EDGE,{"disambiguationData":[OSD([sQuery(id+"F0.wireOp",EDGE,"E2.4.0.2")])],"isStart":false});
            var Q3;
            Q3=makeQuery(id+"F1.opExtrude","CAP_EDGE",EDGE,{"disambiguationData":[OSD([sQuery(id+"F0.wireOp",EDGE,"E2.5.0.2")])],"isStart":false});
            var Q4;
            Q4=makeQuery(id+"F1.opExtrude","CAP_EDGE",EDGE,{"disambiguationData":[OSD([sQuery(id+"F0.wireOp",EDGE,"E2.6.0.2")])],"isStart":false});
            var Q5;
            Q5=makeQuery(id+"F1.opExtrude","CAP_EDGE",EDGE,{"disambiguationData":[OSD([sQuery(id+"F0.wireOp",EDGE,"E2.7.0.2")])],"isStart":false});
            var Q6;
            Q6=makeQuery(id+"F1.opExtrude","CAP_EDGE",EDGE,{"disambiguationData":[OSD([sQuery(id+"F0.wireOp",EDGE,"E2.8.0.2")])],"isStart":false});
            var Q7;
            Q7=makeQuery(id+"F1.opExtrude","CAP_EDGE",EDGE,{"disambiguationData":[OSD([sQuery(id+"F0.wireOp",EDGE,"E2.9.0.2")])],"isStart":false});
            var Q8;
            Q8=makeQuery(id+"F1.opExtrude","CAP_EDGE",EDGE,{"disambiguationData":[OSD([sQuery(id+"F0.wireOp",EDGE,"E3.1.0.2")])],"isStart":false});
            var Q9;
            Q9=makeQuery(id+"F1.opExtrude","CAP_EDGE",EDGE,{"disambiguationData":[OSD([sQuery(id+"F0.wireOp",EDGE,"E3.2.0.2")])],"isStart":false});
            var Q10;
            Q10=makeQuery(id+"F1.opExtrude","CAP_EDGE",EDGE,{"disambiguationData":[OSD([sQuery(id+"F0.wireOp",EDGE,"E3.3.0.2")])],"isStart":false});
            var Q11;
            Q11=makeQuery(id+"F1.opExtrude","CAP_EDGE",EDGE,{"disambiguationData":[OSD([sQuery(id+"F0.wireOp",EDGE,"E3.4.0.2")])],"isStart":false});
            var Q12;
            Q12=makeQuery(id+"F1.opExtrude","CAP_EDGE",EDGE,{"disambiguationData":[OSD([sQuery(id+"F0.wireOp",EDGE,"E3.5.0.2")])],"isStart":false});
            var Q13;
            Q13=makeQuery(id+"F1.opExtrude","CAP_EDGE",EDGE,{"disambiguationData":[OSD([sQuery(id+"F0.wireOp",EDGE,"E3.6.0.2")])],"isStart":false});
            var Q14;
            Q14=makeQuery(id+"F1.opExtrude","CAP_EDGE",EDGE,{"disambiguationData":[OSD([sQuery(id+"F0.wireOp",EDGE,"E3.7.0.2")])],"isStart":false});
            var Q15;
            Q15=makeQuery(id+"F1.opExtrude","CAP_EDGE",EDGE,{"disambiguationData":[OSD([sQuery(id+"F0.wireOp",EDGE,"E3.8.0.2")])],"isStart":false});
            var Q16;
            Q16=makeQuery(id+"F1.opExtrude","CAP_EDGE",EDGE,{"disambiguationData":[OSD([sQuery(id+"F0.wireOp",EDGE,"E3.9.0.2")])],"isStart":false});
            var Q17;
            Q17=makeQuery(id+"F1.opExtrude","CAP_EDGE",EDGE,{"disambiguationData":[OSD([sQuery(id+"F0.wireOp",EDGE,"E4.1.0.2")])],"isStart":false});
            var Q18;
            Q18=makeQuery(id+"F1.opExtrude","CAP_EDGE",EDGE,{"disambiguationData":[OSD([sQuery(id+"F0.wireOp",EDGE,"E4.2.0.2")])],"isStart":false});
            var Q19;
            Q19=makeQuery(id+"F1.opExtrude","CAP_EDGE",EDGE,{"disambiguationData":[OSD([sQuery(id+"F0.wireOp",EDGE,"E4.3.0.2")])],"isStart":false});
            var Q20;
            Q20=makeQuery(id+"F1.opExtrude","CAP_EDGE",EDGE,{"disambiguationData":[OSD([sQuery(id+"F0.wireOp",EDGE,"E4.4.0.2")])],"isStart":false});
            var Q21;
            Q21=makeQuery(id+"F1.opExtrude","CAP_EDGE",EDGE,{"disambiguationData":[OSD([sQuery(id+"F0.wireOp",EDGE,"E4.5.0.2")])],"isStart":false});
            var Q22;
            Q22=makeQuery(id+"F1.opExtrude","CAP_EDGE",EDGE,{"disambiguationData":[OSD([sQuery(id+"F0.wireOp",EDGE,"E4.6.0.2")])],"isStart":false});
            var Q23;
            Q23=makeQuery(id+"F1.opExtrude","CAP_EDGE",EDGE,{"disambiguationData":[OSD([sQuery(id+"F0.wireOp",EDGE,"E4.7.0.2")])],"isStart":false});
            var Q24;
            Q24=makeQuery(id+"F1.opExtrude","CAP_EDGE",EDGE,{"disambiguationData":[OSD([sQuery(id+"F0.wireOp",EDGE,"E4.8.0.2")])],"isStart":false});
            var Q25;
            Q25=makeQuery(id+"F1.opExtrude","CAP_EDGE",EDGE,{"disambiguationData":[OSD([sQuery(id+"F0.wireOp",EDGE,"E4.9.0.2")])],"isStart":false});
            var Q26;
            Q26=makeQuery(id+"F1.opExtrude","CAP_EDGE",EDGE,{"disambiguationData":[OSD([sQuery(id+"F0.wireOp",EDGE,"E5.1.0.2")])],"isStart":false});
            var Q27;
            Q27=makeQuery(id+"F1.opExtrude","CAP_EDGE",EDGE,{"disambiguationData":[OSD([sQuery(id+"F0.wireOp",EDGE,"E5.2.0.2")])],"isStart":false});
            var Q28;
            Q28=makeQuery(id+"F1.opExtrude","CAP_EDGE",EDGE,{"disambiguationData":[OSD([sQuery(id+"F0.wireOp",EDGE,"E5.3.0.2")])],"isStart":false});
            var Q29;
            Q29=makeQuery(id+"F1.opExtrude","CAP_EDGE",EDGE,{"disambiguationData":[OSD([sQuery(id+"F0.wireOp",EDGE,"E5.4.0.2")])],"isStart":false});
            var Q30;
            Q30=makeQuery(id+"F1.opExtrude","CAP_EDGE",EDGE,{"disambiguationData":[OSD([sQuery(id+"F0.wireOp",EDGE,"E5.5.0.2")])],"isStart":false});
            var Q31;
            Q31=makeQuery(id+"F1.opExtrude","CAP_EDGE",EDGE,{"disambiguationData":[OSD([sQuery(id+"F0.wireOp",EDGE,"E5.6.0.2")])],"isStart":false});
            var Q32;
            Q32=makeQuery(id+"F1.opExtrude","CAP_EDGE",EDGE,{"disambiguationData":[OSD([sQuery(id+"F0.wireOp",EDGE,"E5.7.0.2")])],"isStart":false});
            var Q33;
            Q33=makeQuery(id+"F1.opExtrude","CAP_EDGE",EDGE,{"disambiguationData":[OSD([sQuery(id+"F0.wireOp",EDGE,"E5.8.0.2")])],"isStart":false});
            var Q34;
            Q34=makeQuery(id+"F1.opExtrude","CAP_EDGE",EDGE,{"disambiguationData":[OSD([sQuery(id+"F0.wireOp",EDGE,"E5.9.0.2")])],"isStart":false});
            var Q35;
            Q35=makeQuery(id+"F1.opExtrude","CAP_EDGE",EDGE,{"disambiguationData":[OSD([sQuery(id+"F0.wireOp",EDGE,"E6.1.0.2")])],"isStart":false});
            var Q36;
            Q36=makeQuery(id+"F1.opExtrude","CAP_EDGE",EDGE,{"disambiguationData":[OSD([sQuery(id+"F0.wireOp",EDGE,"E6.2.0.2")])],"isStart":false});
            chamfer(context, id + "F6", {"entities" : qUnion([Q0, Q1, Q2, Q3, Q4, Q5, Q6, Q7, Q8, Q9, Q10, Q11, Q12, Q13, Q14, Q15, Q16, Q17, Q18, Q19, Q20, Q21, Q22, Q23, Q24, Q25, Q26, Q27, Q28, Q29, Q30, Q31, Q32, Q33, Q34, Q35, Q36]), "width" : 5.08 * mm, "tangentPropagation" : true});
        }
    });
